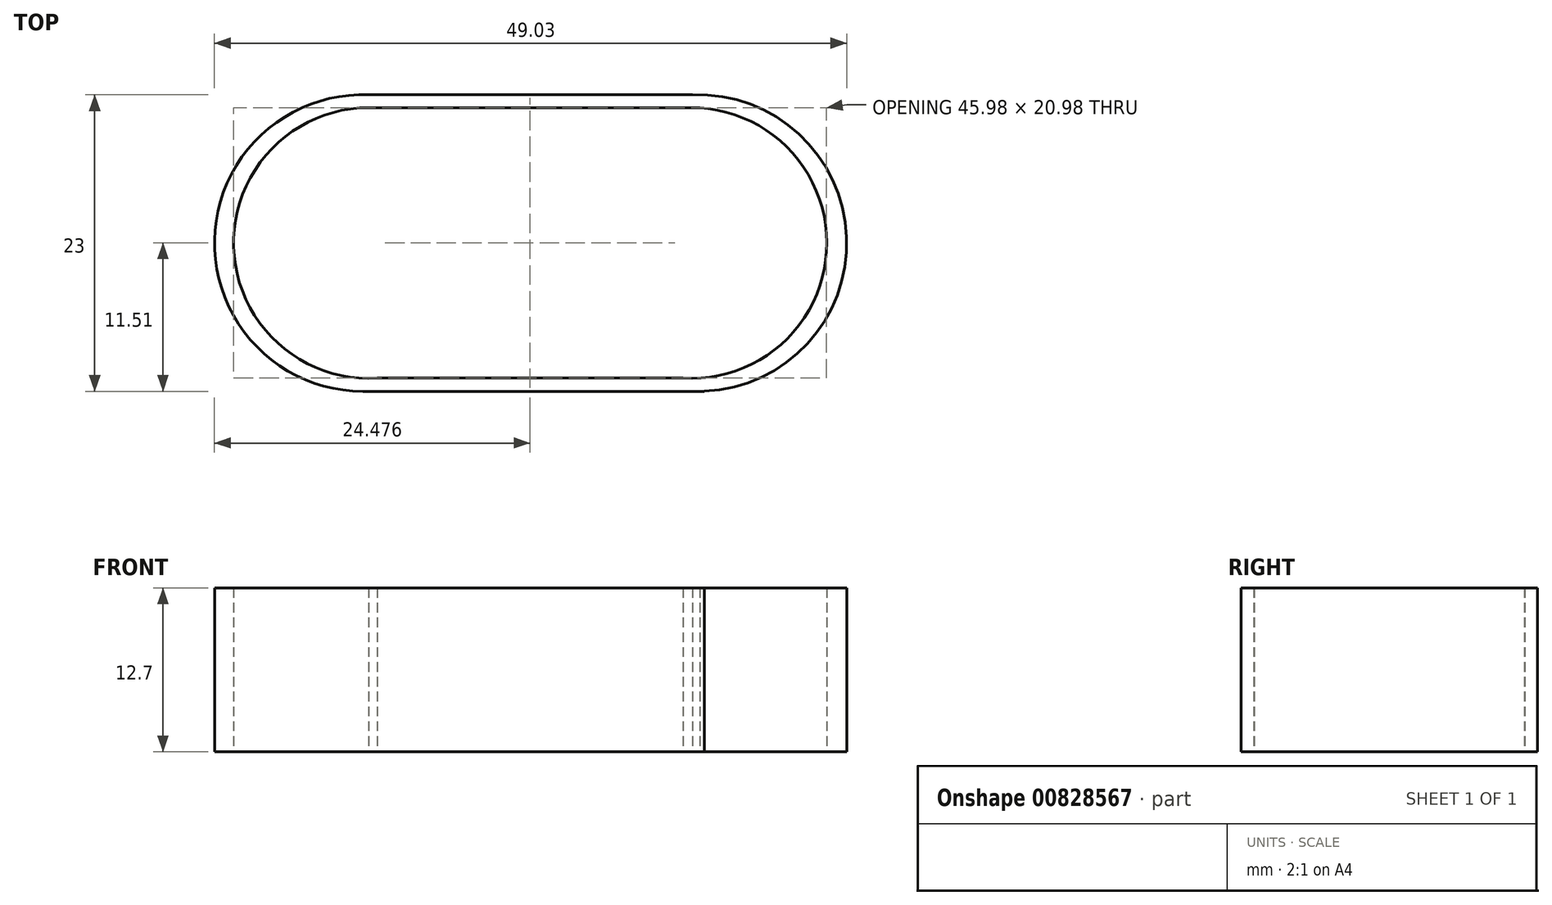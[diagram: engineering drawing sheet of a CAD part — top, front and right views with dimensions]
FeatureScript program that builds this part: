
annotation { "Feature Type Name" : "Feature", "Feature Type Description" : "" }
export const myFeature = defineFeature(function(context is Context, id is Id, definition is map)
    precondition{}
    {
        {
            var Q0;
            Q0=qCreatedBy(makeId("Top.planeOp"),FACE);
            var sketch = newSketch(context, id + "F0", { "sketchPlane" : qUnion([Q0])});
            skCircle(sketch, "E0", {"center": v(-30.73, 0) * mm, "radius": 10.5 * mm});
            skCircle(sketch, "E1", {"center": v(-5.73, 0) * mm, "radius": 10.5 * mm});
            skLineSegment(sketch, "E2.bottom", {"start": v(-30.73, 10.5) * mm, "end": v(-5.09, 10.5) * mm});
            skLineSegment(sketch, "E2.top", {"start": v(-30.73, -10.48) * mm, "end": v(-5.09, -10.48) * mm});
            skLineSegment(sketch, "E2.left", {"start": v(-30.73, 10.5) * mm, "end": v(-30.73, -10.48) * mm});
            skLineSegment(sketch, "E2.right", {"start": v(-5.09, 10.5) * mm, "end": v(-5.09, -10.48) * mm});
            skSolve(sketch);
        }
        {
            var Q0;
            Q0=qCreatedBy(makeId("Top.planeOp"),FACE);
            var sketch = newSketch(context, id + "F1", { "sketchPlane" : qUnion([Q0])});
            skCircle(sketch, "E3", {"center": v(-31.2, 0) * mm, "radius": 11.5 * mm});
            skCircle(sketch, "E4", {"center": v(-5.18, 0) * mm, "radius": 11.5 * mm});
            skLineSegment(sketch, "E5.bottom", {"start": v(-30.98, 11.5) * mm, "end": v(-31.2, 11.5) * mm});
            skLineSegment(sketch, "E5.top", {"start": v(-30.98, -11.5) * mm, "end": v(-31.2, -11.5) * mm});
            skLineSegment(sketch, "E5.left", {"start": v(-30.98, 11.5) * mm, "end": v(-30.98, -11.5) * mm});
            skLineSegment(sketch, "E5.right", {"start": v(-31.2, 11.5) * mm, "end": v(-31.2, -11.5) * mm});
            skLineSegment(sketch, "E6.bottom", {"start": v(-4.72, 11.5) * mm, "end": v(-30.98, 11.5) * mm});
            skLineSegment(sketch, "E6.top", {"start": v(-4.72, -11.5) * mm, "end": v(-30.98, -11.5) * mm});
            skLineSegment(sketch, "E6.left", {"start": v(-4.72, 11.5) * mm, "end": v(-4.72, -11.5) * mm});
            skSolve(sketch);
        }
        {
            var Q0;
            Q0 = qSketchRegion(id + "F1", true);
            extrude(context, id + "F2", {"entities" : qUnion([Q0]), "depth" : 12.7 * mm, "offsetDistance" : 25.4 * mm});
        }
        {
            var Q0;
            Q0 = qSketchRegion(id + "F0", true);
            extrude(context, id + "F3", {"entities" : qUnion([Q0]), "operationType" : NewBodyOperationType.REMOVE, "depth" : 25.4 * mm, "offsetDistance" : 25.4 * mm});
        }
    });
